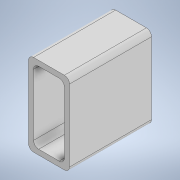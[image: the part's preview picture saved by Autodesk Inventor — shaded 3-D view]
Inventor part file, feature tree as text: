
AUTODESK INVENTOR PART (.ipt)
format: ipt  version: 2020 (Build 240168000, 168)  size: 118,272 bytes
history: native  units: in
note: dims shown in document units (in); Inventor stores cm internally (conversion verified against a paired STEP export)
features: extrude x1, sketch x1
ambient origin geometry x8: Origin, YZ Plane, XZ Plane, XY Plane, X Axis, Y Axis, Z Axis, Center Point
bodies: Solid1 (feature_tree)
feature tree (2):
  extrude  "Extrusion1"  Depth=1.0in
  sketch  "Sketch1"  dims[d0=2.0in d1=1.0in d2=0.125in d3=0.125in d4=0.125in d5=0.125in d6=0.125in d7=0.125in d8=0.125in d9=0.125in d10=0.125in d11=2.0in d12=0.0in]
